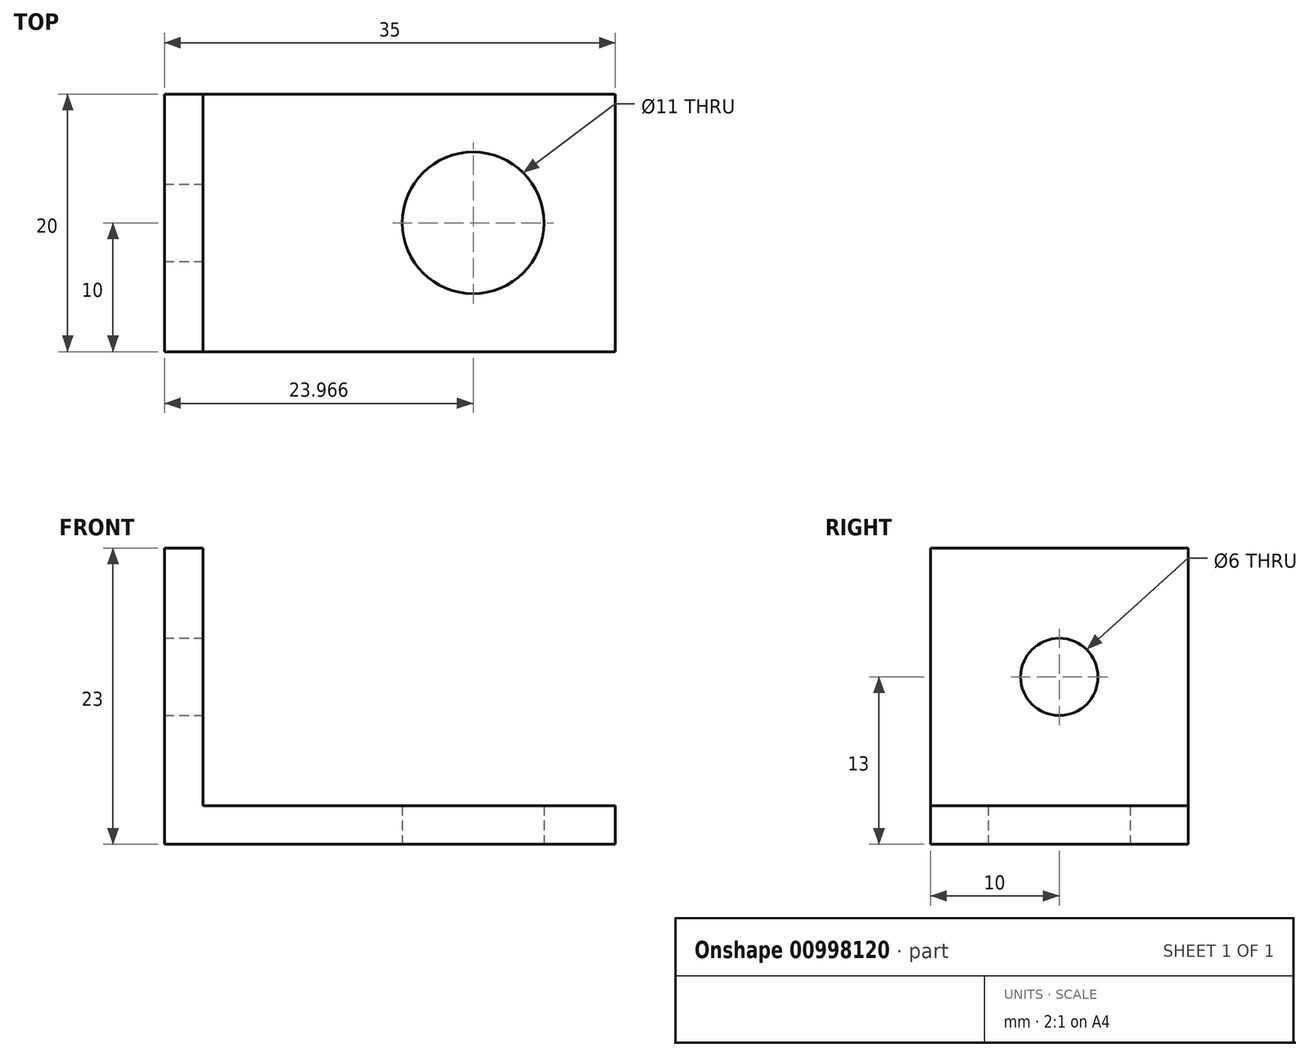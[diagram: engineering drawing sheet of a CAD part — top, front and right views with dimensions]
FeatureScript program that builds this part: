
annotation { "Feature Type Name" : "Feature", "Feature Type Description" : "" }
export const myFeature = defineFeature(function(context is Context, id is Id, definition is map)
    precondition{}
    {
        {
            var Q0;
            Q0=qCreatedBy(makeId("Top.planeOp"),FACE);
            var sketch = newSketch(context, id + "F0", { "sketchPlane" : qUnion([Q0])});
            skLineSegment(sketch, "E0", {"start": v(0, 0) * mm, "end": v(35, 0) * mm, "construction": true});
            skLineSegment(sketch, "E1", {"start": v(0, 0) * mm, "end": v(0, -10) * mm});
            skLineSegment(sketch, "E2", {"start": v(0, -10) * mm, "end": v(35, -10) * mm});
            skLineSegment(sketch, "E3", {"start": v(35, -10) * mm, "end": v(35, 0) * mm});
            skArc(sketch, "E4", {"start": v(18.47, 0) * mm, "mid": v(23.97, -5.5) * mm, "end": v(29.47, 0) * mm});
            skArc(sketch, "E5.MirrorCS", {"start": v(18.47, 0) * mm, "mid": v(23.97, 5.5) * mm, "end": v(29.47, 0) * mm});
            skLineSegment(sketch, "E6.MirrorCS", {"start": v(35, 10) * mm, "end": v(35, 0) * mm});
            skLineSegment(sketch, "E7.MirrorCS", {"start": v(0, 10) * mm, "end": v(35, 10) * mm});
            skLineSegment(sketch, "E8.MirrorCS", {"start": v(0, 0) * mm, "end": v(0, 10) * mm});
            skSolve(sketch);
        }
        {
            var Q0;
            Q0=qSketchRegion(id+"F0",true);
            extrude(context, id + "F1", {"entities" : qUnion([Q0]), "depth" : 3 * mm, "offsetDistance" : 25 * mm});
        }
        {
            var Q0;
            Q0=makeQuery(id+"F1.opExtrude","CAP_FACE",FACE,{"disambiguationData":[OSD([sQuery(id+"F0.wireOp",EDGE,"E1"),sQuery(id+"F0.wireOp",EDGE,"E2"),sQuery(id+"F0.wireOp",EDGE,"E3"),sQuery(id+"F0.wireOp",EDGE,"IYzi4lmI-XeZq-SLUe-WPhh-TTFrGCIOOOSC"),sQuery(id+"F0.wireOp",EDGE,"E4"),sQuery(id+"F0.wireOp",EDGE,"E5.MirrorCS"),sQuery(id+"F0.wireOp",EDGE,"73307338-7fb2-4be3-bc96-a081cc1e89dd0.MirrorCS"),sQuery(id+"F0.wireOp",EDGE,"E6.MirrorCS"),sQuery(id+"F0.wireOp",EDGE,"E7.MirrorCS"),sQuery(id+"F0.wireOp",EDGE,"E8.MirrorCS")])],"isStart":false});
            var sketch = newSketch(context, id + "F2", { "sketchPlane" : qUnion([Q0])});
            skLineSegment(sketch, "E9.bottom", {"start": v(0, 10) * mm, "end": v(3, 10) * mm});
            skLineSegment(sketch, "E9.top", {"start": v(0, -10) * mm, "end": v(3, -10) * mm});
            skLineSegment(sketch, "E9.left", {"start": v(0, 10) * mm, "end": v(0, -10) * mm});
            skLineSegment(sketch, "E9.right", {"start": v(3, 10) * mm, "end": v(3, -10) * mm});
            skSolve(sketch);
        }
        {
            var Q0;
            Q0=qSketchRegion(id+"F2",true);
            extrude(context, id + "F3", {"entities" : qUnion([Q0]), "operationType" : NewBodyOperationType.ADD, "depth" : 20 * mm, "offsetDistance" : 25 * mm});
        }
        {
            var Q0;
            Q0=makeQuery(id+"F3.opExtrude","SWEPT_FACE",FACE,{"disambiguationData":[OSD([sQuery(id+"F2.wireOp",EDGE,"E9.right")])]});
            var sketch = newSketch(context, id + "F4", { "sketchPlane" : qUnion([Q0])});
            skLineSegment(sketch, "E10", {"start": v(0, 23) * mm, "end": v(0, 3) * mm, "construction": true});
            skLineSegment(sketch, "E11", {"start": v(-10, 13) * mm, "end": v(10, 13) * mm, "construction": true});
            skCircle(sketch, "E12", {"center": v(0, 13) * mm, "radius": 3 * mm});
            skSolve(sketch);
        }
        {
            var Q0;
            Q0=makeQuery(id+"F4.imprint","IMPRINT",FACE,{"disambiguationData":[TD([[makeQuery(id+"F4.imprint","IMPRINT",EDGE,{"derivedFrom":sQuery(id+"F4.wireOp",EDGE,"E12")}),1.0]])]});
            extrude(context, id + "F5", {"entities" : qUnion([Q0]), "operationType" : NewBodyOperationType.REMOVE, "endBound" : BoundingType.THROUGH_ALL, "oppositeDirection" : true, "depth" : 25 * mm, "offsetDistance" : 25 * mm});
        }
    });
